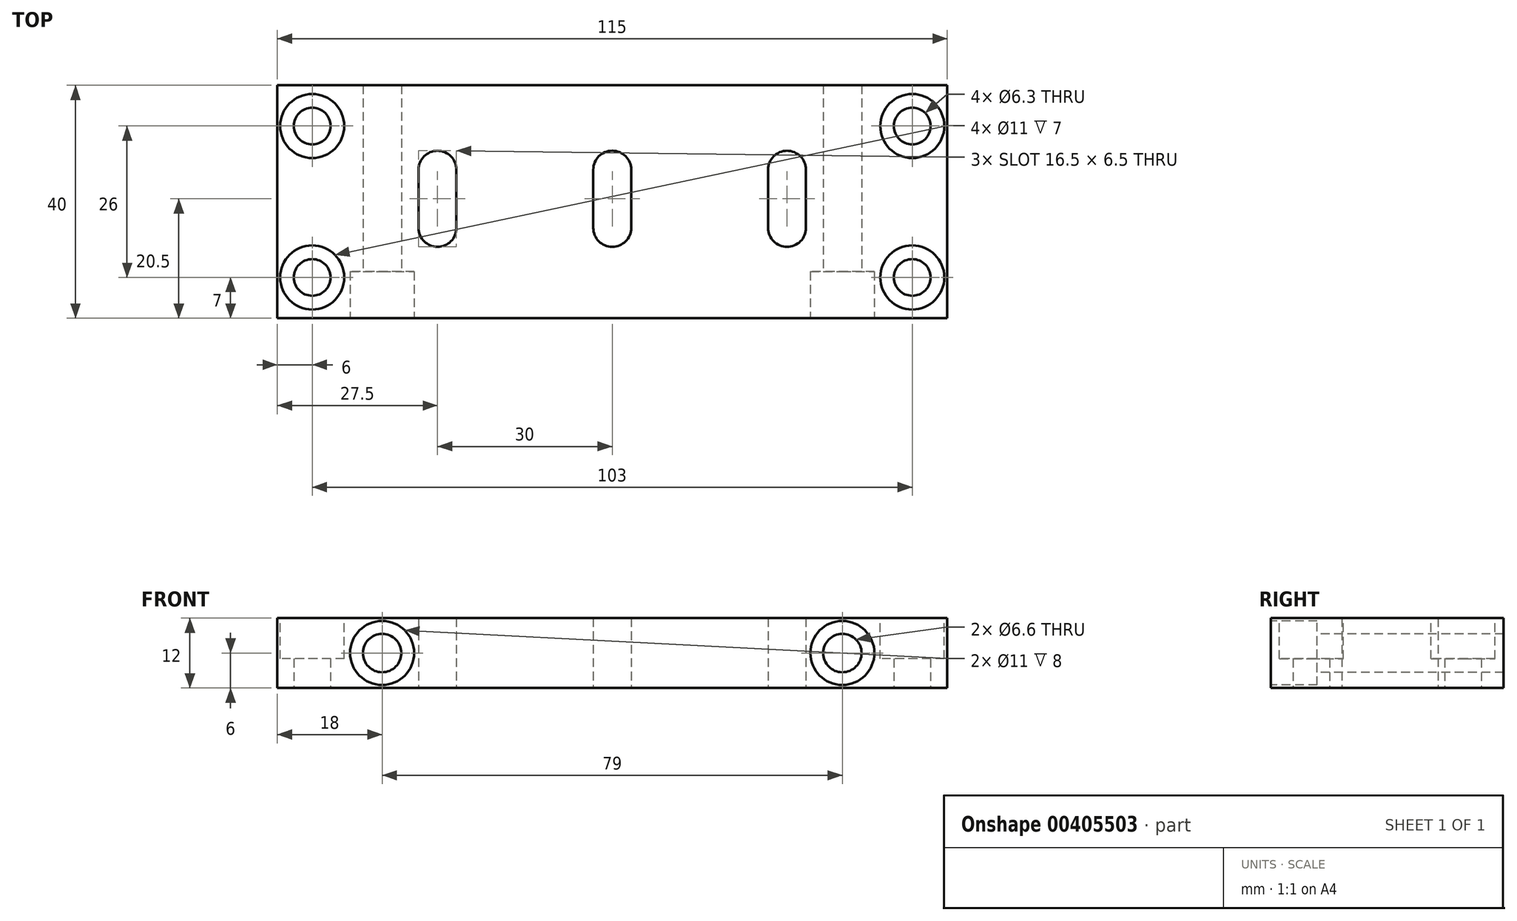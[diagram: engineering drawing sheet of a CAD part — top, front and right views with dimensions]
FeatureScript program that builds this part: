
annotation { "Feature Type Name" : "Feature", "Feature Type Description" : "" }
export const myFeature = defineFeature(function(context is Context, id is Id, definition is map)
    precondition{}
    {
        {
            var Q0;
            Q0=qCreatedBy(makeId("Top.planeOp"),FACE);
            var sketch = newSketch(context, id + "F0", { "sketchPlane" : qUnion([Q0])});
            skLineSegment(sketch, "E0.bottom", {"start": v(0, 0) * mm, "end": v(115, 0) * mm});
            skLineSegment(sketch, "E0.top", {"start": v(0, -40) * mm, "end": v(115, -40) * mm});
            skLineSegment(sketch, "E0.left", {"start": v(0, 0) * mm, "end": v(0, -40) * mm});
            skLineSegment(sketch, "E0.right", {"start": v(115, 0) * mm, "end": v(115, -40) * mm});
            skSolve(sketch);
        }
        {
            var Q0;
            Q0 = qSketchRegion(id + "F0", true);
            extrude(context, id + "F1", {"entities" : qUnion([Q0]), "depth" : 12 * mm});
        }
        {
            var Q0;
            Q0=qCreatedBy(makeId("Top.planeOp"),FACE);
            var sketch = newSketch(context, id + "F2", { "sketchPlane" : qUnion([Q0])});
            skLineSegment(sketch, "E1", {"start": v(30.75, -14.5) * mm, "end": v(30.75, -24.5) * mm});
            skLineSegment(sketch, "E2", {"start": v(24.25, -24.5) * mm, "end": v(24.25, -14.5) * mm});
            skLineSegment(sketch, "E3", {"start": v(54.25, -14.5) * mm, "end": v(54.25, -24.5) * mm});
            skLineSegment(sketch, "E4", {"start": v(60.75, -24.5) * mm, "end": v(60.75, -14.5) * mm});
            skLineSegment(sketch, "E5", {"start": v(84.25, -14.5) * mm, "end": v(84.25, -24.5) * mm});
            skLineSegment(sketch, "E6", {"start": v(90.75, -24.5) * mm, "end": v(90.75, -14.5) * mm});
            skLineSegment(sketch, "E7", {"start": v(30.75, -14.5) * mm, "end": v(90.75, -14.5) * mm, "construction": true});
            skLineSegment(sketch, "E8", {"start": v(24.25, -24.5) * mm, "end": v(90.75, -24.5) * mm, "construction": true});
            skArc(sketch, "E9", {"start": v(30.75, -14.5) * mm, "mid": v(27.5, -11.25) * mm, "end": v(24.25, -14.5) * mm});
            skArc(sketch, "E10", {"start": v(60.75, -14.5) * mm, "mid": v(57.5, -11.25) * mm, "end": v(54.25, -14.5) * mm});
            skArc(sketch, "E11", {"start": v(54.25, -24.5) * mm, "mid": v(57.5, -27.75) * mm, "end": v(60.75, -24.5) * mm});
            skArc(sketch, "E12", {"start": v(24.25, -24.5) * mm, "mid": v(27.5, -27.75) * mm, "end": v(30.75, -24.5) * mm});
            skArc(sketch, "E13", {"start": v(84.25, -24.5) * mm, "mid": v(87.5, -27.75) * mm, "end": v(90.75, -24.5) * mm});
            skArc(sketch, "E14", {"start": v(90.75, -14.5) * mm, "mid": v(87.5, -11.25) * mm, "end": v(84.25, -14.5) * mm});
            skSolve(sketch);
        }
        {
            var Q0;
            Q0 = qSketchRegion(id + "F2", true);
            extrude(context, id + "F3", {"entities" : qUnion([Q0]), "operationType" : NewBodyOperationType.REMOVE, "depth" : 12.1 * mm});
        }
        {
            var Q0;
            Q0=qCreatedBy(makeId("Top.planeOp"),FACE);
            var sketch = newSketch(context, id + "F4", { "sketchPlane" : qUnion([Q0])});
            skCircle(sketch, "E15", {"center": v(6, -7) * mm, "radius": 3.15 * mm});
            skCircle(sketch, "E16", {"center": v(6, -33) * mm, "radius": 3.15 * mm});
            skCircle(sketch, "E17", {"center": v(109, -7) * mm, "radius": 3.15 * mm});
            skCircle(sketch, "E18", {"center": v(109, -33) * mm, "radius": 3.15 * mm});
            skLineSegment(sketch, "E19", {"start": v(6, -7) * mm, "end": v(6, -33) * mm, "construction": true});
            skLineSegment(sketch, "E20", {"start": v(6, -33) * mm, "end": v(109, -33) * mm, "construction": true});
            skLineSegment(sketch, "E21", {"start": v(109, -33) * mm, "end": v(109, -7) * mm});
            skLineSegment(sketch, "E22", {"start": v(109, -7) * mm, "end": v(6, -7) * mm, "construction": true});
            skSolve(sketch);
        }
        {
            var Q0;
            Q0 = qSketchRegion(id + "F4", true);
            extrude(context, id + "F5", {"entities" : qUnion([Q0]), "operationType" : NewBodyOperationType.REMOVE, "depth" : 12.1 * mm});
        }
        {
            var Q0;
            Q0=makeQuery(id+"F1.opExtrude","CAP_FACE",FACE,{"disambiguationData":[OSD([sQuery(id+"F0.wireOp",EDGE,"E0.bottom"),sQuery(id+"F0.wireOp",EDGE,"E0.top"),sQuery(id+"F0.wireOp",EDGE,"E0.left"),sQuery(id+"F0.wireOp",EDGE,"E0.right")])],"isStart":false});
            var sketch = newSketch(context, id + "F6", { "sketchPlane" : qUnion([Q0])});
            skCircle(sketch, "E23", {"center": v(6, -7) * mm, "radius": 5.5 * mm});
            skCircle(sketch, "E24", {"center": v(6, -33) * mm, "radius": 5.5 * mm});
            skCircle(sketch, "E25", {"center": v(109, -7) * mm, "radius": 5.5 * mm});
            skCircle(sketch, "E26", {"center": v(109, -33) * mm, "radius": 5.5 * mm});
            skLineSegment(sketch, "E27", {"start": v(6, -7) * mm, "end": v(6, -33) * mm, "construction": true});
            skLineSegment(sketch, "E28", {"start": v(6, -33) * mm, "end": v(109, -33) * mm, "construction": true});
            skLineSegment(sketch, "E29", {"start": v(109, -33) * mm, "end": v(109, -7) * mm, "construction": true});
            skLineSegment(sketch, "E30", {"start": v(109, -7) * mm, "end": v(6, -7) * mm, "construction": true});
            skSolve(sketch);
        }
        {
            var Q0;
            Q0 = qSketchRegion(id + "F6", true);
            extrude(context, id + "F7", {"entities" : qUnion([Q0]), "operationType" : NewBodyOperationType.REMOVE, "oppositeDirection" : true, "depth" : 7 * mm});
        }
        {
            var Q0;
            Q0=makeQuery(id+"F1.opExtrude","SWEPT_FACE",FACE,{"disambiguationData":[OSD([sQuery(id+"F0.wireOp",EDGE,"E0.top")])]});
            var sketch = newSketch(context, id + "F8", { "sketchPlane" : qUnion([Q0])});
            skLineSegment(sketch, "E31", {"start": v(97, 6) * mm, "end": v(18, 6) * mm, "construction": true});
            skCircle(sketch, "E32", {"center": v(97, 6) * mm, "radius": 3.3 * mm});
            skCircle(sketch, "E33", {"center": v(18, 6) * mm, "radius": 3.3 * mm});
            skSolve(sketch);
        }
        {
            var Q0;
            Q0 = qSketchRegion(id + "F8", true);
            extrude(context, id + "F9", {"entities" : qUnion([Q0]), "operationType" : NewBodyOperationType.REMOVE, "oppositeDirection" : true, "depth" : 40.1 * mm});
        }
        {
            var Q0;
            Q0=makeQuery(id+"F1.opExtrude","SWEPT_FACE",FACE,{"disambiguationData":[OSD([sQuery(id+"F0.wireOp",EDGE,"E0.top")])]});
            var sketch = newSketch(context, id + "F10", { "sketchPlane" : qUnion([Q0])});
            skLineSegment(sketch, "E34", {"start": v(97, 6) * mm, "end": v(18, 6) * mm, "construction": true});
            skCircle(sketch, "E35", {"center": v(18, 6) * mm, "radius": 5.5 * mm});
            skCircle(sketch, "E36", {"center": v(97, 6) * mm, "radius": 5.5 * mm});
            skSolve(sketch);
        }
        {
            var Q0;
            Q0 = qSketchRegion(id + "F10", true);
            extrude(context, id + "F11", {"entities" : qUnion([Q0]), "operationType" : NewBodyOperationType.REMOVE, "oppositeDirection" : true, "depth" : 8 * mm});
        }
    });
